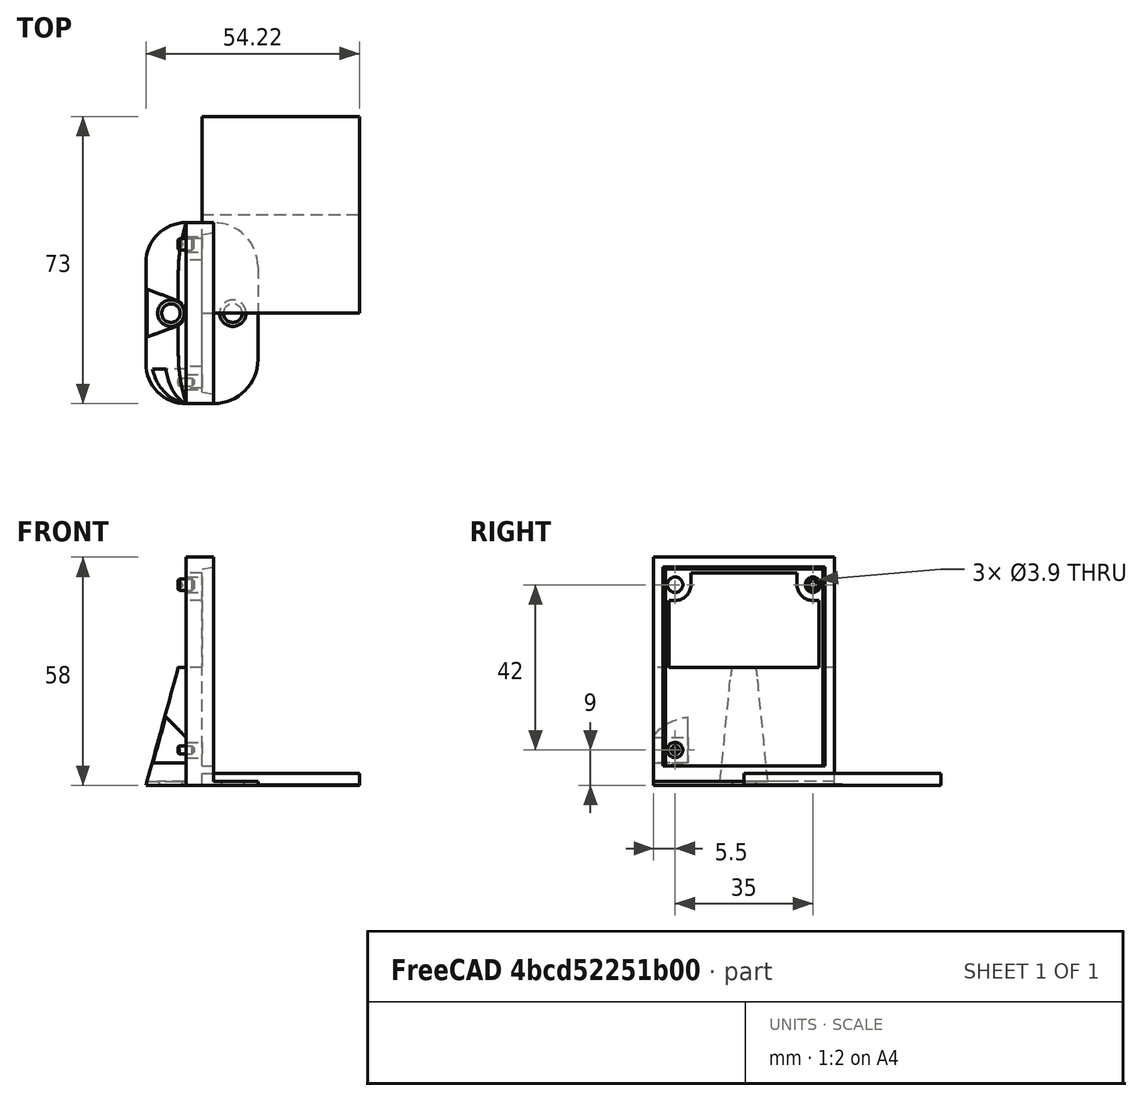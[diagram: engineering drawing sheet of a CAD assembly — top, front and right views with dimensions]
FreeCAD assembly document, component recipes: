
FREECAD ASSEMBLY — COMPONENT RECIPES ("HorizonMirror")

This assembly document has 2 components, labeled P0..P1 below (a component is one placed body or linked part). 1 of them carries a construction recipe — the FreeCAD feature program that regenerates the part from scratch, quoted from this document or its linked companion documents; the rest are supplied as boundary geometry only. No exploded tour is included for this assembly.
COMPONENT P0 — geometry summary ("Mirror"; no construction recipe available for this part):
  bounding box: 50.0 x 40.0 x 3.0 mm
  tessellated surface: 44 triangles
  volume: 6100 mm^3 (102% of its bounding box)
  symmetry: 2-fold rotationally symmetric about the x axis; 2-fold rotationally symmetric about the y axis; 2-fold rotationally symmetric about the z axis; mirror-symmetric across its x mid-plane, y mid-plane, z mid-plane
COMPONENT P1 — recipe-attached ("HorizonMirrorFrame", modeled in this document).
Construction recipe (the document's own serialized feature program — sketch geometry with constraints, then the solid features built on it; lengths are millimeters unless a unit is written):

FEATURE [PartDesign::Plane] DatumPlane  label="Plane_BaseBottom"
  AttachmentSupport = -> [XY_Plane004]
  Length = 60
  MapMode = 5
  ResizeMode = 0
  Width = 60
FEATURE [PartDesign::Plane] DatumPlane001  label="Plane_BaseTop"
  AttachmentOffset = pos=(0,0,1) rot=(0,0,1;0rad)
  AttachmentSupport = -> [DatumPlane]
  Length = 60
  MapMode = 5
  Placement = pos=(0,0,1) rot=(0,0,1;0rad)
  ResizeMode = 0
  Width = 60
  expr: .AttachmentOffset.Base.z = <<Dimensions>>.horizon_mirror_base_thickness
FEATURE [Sketcher::SketchObject] Sketch
  ArcFitTolerance = 0
  AttachmentSupport = -> [DatumPlane001]
  FullyConstrained = true
  MakeInternals = false
  MapMode = 5
  Placement = pos=(0,0,1) rot=(0,0,1;0rad)
  expr: Constraints[0] = <<Dimensions>>.horizon_mirror_screw_diameter
  expr: Constraints[5] = <<Dimensions>>.horizon_mirror_countersink_diameter * 0.5 + <<Dimensions>>.horizon_mirror_base_width + <<Dimensions>>.horizon_mirror_mirror_thickness * 0.5
  sketch-geometry (2):
    g0: Circle CenterX=-7.86 CenterY=0 CenterZ=0 NormalX=0 NormalY=0 NormalZ=1 AngleXU=0 Radius=1.5
    g1: Circle CenterX=7.86 CenterY=0 CenterZ=0 NormalX=0 NormalY=0 NormalZ=1 AngleXU=0 Radius=1.5
  constraints (6):
    c: Diameter(g0) = 3
    c: Equal(g0,g1)
    c: PointOnObject(g0,g-1)
    c: Symmetric(g0,g1,g-1)
    c: Distance(g0,g1) = 15.72  'hole_distance'
    c: Distance(g-1,g0) = 7.86
FEATURE [PartDesign::Plane] DatumPlane002  label="Plane_MirrorBack"
  AttachmentSupport = -> [YZ_Plane004]
  Length = 60
  MapMode = 2
  Placement = pos=(0,0,0) rot=(0.57735,0.57735,0.57735;2.0944rad)
  ResizeMode = 0
  Width = 60
FEATURE [PartDesign::Plane] DatumPlane003  label="Plane_FrameFront"
  AttachmentOffset = pos=(0,0,3) rot=(0,0,1;0rad)
  AttachmentSupport = -> [DatumPlane002]
  Length = 60
  MapMode = 5
  Placement = pos=(3,0,0) rot=(0.57735,0.57735,0.57735;2.0944rad)
  ResizeMode = 0
  Width = 60
  expr: .AttachmentOffset.Base.z = <<Dimensions>>.horizon_mirror_mirror_thickness
FEATURE [PartDesign::Plane] DatumPlane004  label="Plane_FrameBack"
  AttachmentOffset = pos=(0,0,-7) rot=(0,0,1;0rad)
  AttachmentSupport = -> [DatumPlane003]
  Length = 60
  MapMode = 5
  Placement = pos=(-4,0,0) rot=(0.57735,0.57735,0.57735;2.0944rad)
  ResizeMode = 0
  Width = 60
  expr: .AttachmentOffset.Base.z = -<<Dimensions>>.mirror_frame_thickness
FEATURE [Sketcher::SketchObject] Sketch001  label="Sketch_Base"
  ArcFitTolerance = 0
  AttachmentSupport = -> [DatumPlane]
  ExternalGeometry = -> [Sketch,DatumPlane004,DatumPlane003]
  FullyConstrained = true
  MakeInternals = false
  MapMode = 5
  expr: Constraints[10] = <<Dimensions>>.horizon_mirror_mirror_width + 2 * <<Dimensions>>.mirror_frame_width
  expr: Constraints[15] = <<Dimensions>>.horizon_mirror_countersink_diameter / 2 + <<Dimensions>>.horizon_mirror_base_width
  expr: Constraints[19] = <<Dimensions>>.horizon_mirror_countersink_diameter / 2 + <<Dimensions>>.horizon_mirror_base_width
  sketch-geometry (11):
    g0: LineSegment StartX=14.22 StartY=11.78 StartZ=0 EndX=14.22 EndY=-11.78 EndZ=0
    g1: GeomPoint [constr] X=-4 Y=23 Z=0
    g2: LineSegment StartX=-4 StartY=-23 StartZ=0 EndX=3 EndY=-23 EndZ=0
    g3: LineSegment StartX=-4 StartY=23 StartZ=0 EndX=3 EndY=23 EndZ=0
    g4: ArcOfCircle CenterX=3 CenterY=-11.78 CenterZ=0 NormalX=0 NormalY=0 NormalZ=1 AngleXU=0 Radius=11.22 StartAngle=4.71239 EndAngle=6.28319
    g5: ArcOfCircle CenterX=3 CenterY=11.78 CenterZ=0 NormalX=0 NormalY=0 NormalZ=1 AngleXU=0 Radius=11.22 StartAngle=0 EndAngle=1.5708
    g6: LineSegment StartX=-14.22 StartY=12.78 StartZ=0 EndX=-14.22 EndY=-12.78 EndZ=0
    g7: ArcOfCircle CenterX=-4 CenterY=12.78 CenterZ=0 NormalX=0 NormalY=0 NormalZ=1 AngleXU=0 Radius=10.22 StartAngle=1.5708 EndAngle=3.14159
    g8: ArcOfCircle CenterX=-4 CenterY=-12.78 CenterZ=0 NormalX=0 NormalY=0 NormalZ=1 AngleXU=0 Radius=10.22 StartAngle=3.14159 EndAngle=4.71239
    g9: LineSegment StartX=3 StartY=23 StartZ=0 EndX=3 EndY=-23 EndZ=0
    g10: LineSegment StartX=-4 StartY=23 StartZ=0 EndX=-4 EndY=-23 EndZ=0
  constraints (24):
    c: Horizontal(g2)
    c: Coincident(g3,g1)
    c: PointOnObject(g3,g-5)
    c: PointOnObject(g2,g-5)
    c: Tangent(g0,g4) = 1.5708
    c: Tangent(g2,g4) = -1.5708
    c: Tangent(g0,g5) = 1.5708
    c: Tangent(g3,g5) = 1.5708
    c: Vertical(g0)
    c: Equal(g5,g4)
    c: DistanceY(g2,g3) = 46
    c: PointOnObject(g2,g-6)
    c: Vertical(g6)
    c: Tangent(g6,g7) = -1.5708
    c: Tangent(g6,g8) = -1.5708
    c: DistanceX(g6,g-3) = 6.36
    c: Symmetric(g3,g2,g-1)
    c: Tangent(g7,g3) = 1.5708
    c: Tangent(g8,g2) = -1.5708
    c: DistanceX(g-4,g0) = 6.36
    c: Coincident(g9,g3)
    c: Coincident(g9,g2)
    c: Coincident(g10,g3)
    c: Coincident(g10,g2)
FEATURE [PartDesign::SubShapeBinder] Binder001  label="Binder_AdjustmentScrew"
  BindCopyOnChange = 0
  BindMode = 0
  ClaimChildren = false
  Context = -> Part001 [Body001.Hole001.Binder001.]
  Fuse = false
  MakeFace = true
  OffsetFill = false
  OffsetIntersection = false
  OffsetJoinType = 0
  OffsetOpenResult = false
  PartialLoad = false
  Relative = true
  Support = -> [Sketch006]
  _Version = 2
FEATURE [PartDesign::Plane] DatumPlane006  label="Plane_Top"
  AttachmentOffset = pos=(0,0,58) rot=(0,0,1;0rad)
  AttachmentSupport = -> [XY_Plane004]
  Length = 60
  MapMode = 5
  Placement = pos=(0,0,58) rot=(0,0,1;0rad)
  ResizeMode = 0
  Width = 60
  expr: .AttachmentOffset.Base.z = <<Dimensions>>.horizon_mirror_mirror_offset + <<Dimensions>>.horizon_mirror_mirror_height + <<Dimensions>>.mirror_frame_width
FEATURE [Sketcher::SketchObject] Sketch010  label="Sketch_ScrewAccess"
  ArcFitTolerance = 0
  AttachmentSupport = -> [DatumPlane001]
  ExternalGeometry = -> [Sketch]
  FullyConstrained = true
  MakeInternals = false
  MapMode = 5
  Placement = pos=(0,0,1) rot=(0,0,1;0rad)
  expr: Constraints[5] = <<Dimensions>>.horizon_mirror_countersink_diameter / 2 + <<Dimensions>>.clearance_loose_fit
  sketch-geometry (4):
    g0: LineSegment StartX=-26.6253 StartY=10.6717 StartZ=0 EndX=-6.62531 EndY=3.39229 EndZ=0
    g1: ArcOfCircle CenterX=-7.86 CenterY=0 CenterZ=0 NormalX=0 NormalY=0 NormalZ=1 AngleXU=0 Radius=3.61 StartAngle=5.06145 EndAngle=7.50492
    g2: LineSegment StartX=-6.62531 StartY=-3.39229 StartZ=0 EndX=-26.6253 EndY=-10.6717 EndZ=0
    g3: LineSegment StartX=-26.6253 StartY=-10.6717 StartZ=0 EndX=-26.6253 EndY=10.6717 EndZ=0
  constraints (9):
    c: Tangent(g0,g1) = 1.5708
    c: Tangent(g1,g2) = 1.5708
    c: Coincident(g2,g3)
    c: Coincident(g3,g0)
    c: Coincident(g1,g-3)
    c: Radius(g1) = 3.61
    c: DistanceX(g0,g0) = 20
    c: Symmetric(g2,g0,g-1)
    c: Angle(g0,g2) = 0.698132
FEATURE [PartDesign::SubShapeBinder] Binder005  label="Binder_BaseFront"
  BindCopyOnChange = 0
  BindMode = 0
  ClaimChildren = false
  Context = -> <external Sextant.FCStd>#Assembly [HorizonMirror.Base.Body001.Binder005.]
  Fuse = false
  MakeFace = true
  OffsetFill = false
  OffsetIntersection = false
  OffsetJoinType = 0
  OffsetOpenResult = false
  PartialLoad = false
  Relative = true
  Support = -> [Sketch001[Edge3,Edge2,Edge1,Edge9]]
  _Version = 2
FEATURE [PartDesign::Plane] DatumPlane007  label="Plane_ViewCenter"
  AttachmentOffset = pos=(0,0,30) rot=(0,0,1;0rad)
  AttachmentSupport = -> [XY_Plane004]
  Length = 60
  MapMode = 5
  Placement = pos=(0,0,30) rot=(0,0,1;0rad)
  ResizeMode = 0
  Width = 60
  expr: .AttachmentOffset.Base.z = <<Dimensions>>.view_center_offset_hor
FEATURE [Sketcher::SketchObject] Sketch009  label="Sketch_LoftTop"
  ArcFitTolerance = 0
  AttachmentSupport = -> [DatumPlane007]
  ExternalGeometry = -> [DatumPlane004,DatumPlane003]
  FullyConstrained = true
  MakeInternals = false
  MapMode = 5
  Placement = pos=(0,0,30) rot=(0,0,1;0rad)
  expr: Constraints[2] = <<Dimensions>>.horizon_mirror_mirror_width + 2 * <<Dimensions>>.mirror_frame_width
  sketch-geometry (4):
    g0: LineSegment StartX=-4 StartY=23 StartZ=0 EndX=-4 EndY=-23 EndZ=0
    g1: LineSegment StartX=-6 StartY=10 StartZ=0 EndX=-6 EndY=-10 EndZ=0
    g2: ArcOfCircle CenterX=37.25 CenterY=10 CenterZ=0 NormalX=0 NormalY=0 NormalZ=1 AngleXU=0 Radius=43.25 StartAngle=2.83629 EndAngle=3.14159
    g3: ArcOfCircle CenterX=37.25 CenterY=-10 CenterZ=0 NormalX=0 NormalY=0 NormalZ=1 AngleXU=0 Radius=43.25 StartAngle=3.14159 EndAngle=3.44689
  constraints (10):
    c: PointOnObject(g2,g-3)
    c: Symmetric(g2,g3,g-1)
    c: Distance(g0) = 46
    c: Symmetric(g1,g1,g-1)
    c: Tangent(g2,g1) = -1.5708
    c: Tangent(g3,g1) = -1.5708
    c: DistanceY(g1,g1) = 20
    c: DistanceX(g1,g3) = 2
    c: Coincident(g0,g3)
    c: Coincident(g2,g0)
FEATURE [PartDesign::SubShapeBinder] Binder006  label="Binder_FrameBase"
  BindCopyOnChange = 0
  BindMode = 0
  ClaimChildren = false
  Context = -> <external Sextant.FCStd>#Assembly [HorizonMirror.Base.Body001.Binder006.]
  Fuse = false
  MakeFace = true
  OffsetFill = false
  OffsetIntersection = false
  OffsetJoinType = 0
  OffsetOpenResult = false
  PartialLoad = false
  Relative = true
  Support = -> [Sketch001[Edge10,Edge8,Edge9,Edge4]]
  _Version = 2
FEATURE [PartDesign::Pad] Pad006  label="Pad_Frame"
  Direction = (0,0,1)
  Length = 10
  Length2 = 10
  Profile = -> Binder006 [Face1]
  Suppressed = false
  Type = 3
  UpToFace = -> DatumPlane006
FEATURE [PartDesign::Pad] Pad007  label="Pad_BaseFront"
  BaseFeature = -> Pad006
  Direction = (0,0,1)
  Length = 10
  Length2 = 10
  Profile = -> Binder005 [Face1]
  Suppressed = false
  Type = 3
  UpToFace = -> DatumPlane001
FEATURE [PartDesign::SubShapeBinder] Binder004  label="Binder_BaseBack"
  BindCopyOnChange = 0
  BindMode = 0
  ClaimChildren = false
  Context = -> Part001 [Body001.Binder004.]
  Fuse = false
  MakeFace = true
  OffsetFill = false
  OffsetIntersection = false
  OffsetJoinType = 0
  OffsetOpenResult = false
  PartialLoad = false
  Relative = true
  Support = -> [Sketch001[Edge7,Edge10,Edge6,Edge5]]
  _Version = 2
FEATURE [PartDesign::AdditiveLoft] AdditiveLoft  label="Loft_BackSupport"
  BaseFeature = -> Pad007
  Closed = false
  Profile = -> Binder004 [Face1]
  Ruled = false
  Sections = -> [Sketch009]
  Suppressed = false
FEATURE [PartDesign::Pocket] Pocket002  label="Pocket_ScrewAccess"
  BaseFeature = -> AdditiveLoft
  Direction = (0,0,-1)
  Length = 5
  Length2 = 5
  Profile = -> Sketch010
  ReferenceAxis = -> Sketch010 [N_Axis]
  Reversed = true
  Suppressed = false
  Type = 1
FEATURE [PartDesign::Hole] Hole  label="Hole_Attachment"
  BaseFeature = -> Pocket002
  CustomThreadClearance = 0
  Depth = 86.1294
  DepthType = 1
  Diameter = 3.4
  DrillForDepth = false
  DrillPoint = 1
  DrillPointAngle = 118
  HoleCutCountersinkAngle = 90
  HoleCutCustomValues = false
  HoleCutDepth = 0
  HoleCutDiameter = 6.72
  HoleCutType = 2
  ModelThread = false
  Profile = -> Sketch
  Suppressed = false
  Tapered = false
  TaperedAngle = 90
  ThreadClass = 0
  ThreadDepth = 86.1294
  ThreadDepthType = 0
  ThreadDirection = 0
  ThreadFit = 0
  ThreadSize = 9
  ThreadType = 1
  Threaded = false
  UseCustomThreadClearance = false
  expr: HoleCutDiameter = <<Dimensions>>.horizon_mirror_countersink_diameter
  expr: ThreadSize = <<Dimensions>>.horizon_mirror_screw_type
FEATURE [Sketcher::SketchObject] Sketch015  label="Sketch_Mirror"
  ArcFitTolerance = 0
  AttachmentSupport = -> [DatumPlane002]
  ExternalGeometry = -> [DatumPlane007]
  FullyConstrained = true
  MakeInternals = false
  MapMode = 5
  Placement = pos=(0,0,0) rot=(0.57735,0.57735,0.57735;2.0944rad)
  expr: Constraints[5] = <<Dimensions>>.horizon_mirror_mirror_offset
  expr: Constraints[8] = <<Dimensions>>.horizon_mirror_mirror_width
  expr: Constraints[9] = <<Dimensions>>.horizon_mirror_mirror_height
  sketch-geometry (7):
    g0: LineSegment StartX=-20 StartY=55 StartZ=0 EndX=20 EndY=55 EndZ=0
    g1: LineSegment StartX=20 StartY=5 StartZ=0 EndX=-20 EndY=5 EndZ=0
    g2: LineSegment StartX=-20 StartY=30 StartZ=0 EndX=20 EndY=30 EndZ=0
    g3: LineSegment StartX=-20 StartY=5 StartZ=0 EndX=-20 EndY=30 EndZ=0
    g4: LineSegment StartX=-20 StartY=30 StartZ=0 EndX=-20 EndY=55 EndZ=0
    g5: LineSegment StartX=20 StartY=55 StartZ=0 EndX=20 EndY=30 EndZ=0
    g6: LineSegment StartX=20 StartY=30 StartZ=0 EndX=20 EndY=5 EndZ=0
  constraints (19):
    c: Coincident(g0,g5)
    c: Coincident(g6,g1)
    c: Coincident(g1,g3)
    c: Coincident(g4,g0)
    c: Horizontal(g1)
    c: DistanceY(g-1,g6) = 5
    c: PointOnObject(g2,g-3)
    c: Symmetric(g0,g0,g-2)
    c: DistanceX(g0,g0) = 40
    c: DistanceY(g3,g4) = 50
    c: Coincident(g3,g4)
    c: Vertical(g3)
    c: Vertical(g4)
    c: Coincident(g5,g6)
    c: Vertical(g5)
    c: Vertical(g6)
    c: Coincident(g3,g2)
    c: Coincident(g5,g2)
    c: PointOnObject(g2,g-3)
FEATURE [Sketcher::SketchObject] Sketch006  label="Sketch_Clips"
  ArcFitTolerance = 0
  AttachmentSupport = -> [DatumPlane004]
  ExternalGeometry = -> [Sketch015]
  FullyConstrained = true
  MakeInternals = false
  MapMode = 5
  Placement = pos=(-4,0,0) rot=(0.57735,0.57735,0.57735;2.0944rad)
  expr: Constraints[0] = <<Dimensions>>.mirror_adjustment_screw_diameter
  expr: Constraints[22] = <<Dimensions>>.mirror_clip_edge_distance + <<Dimensions>>.mirror_clip_width / 2
  expr: Constraints[28] = <<Dimensions>>.mirror_clip_edge_distance
  sketch-geometry (10):
    g0: Circle CenterX=17.5 CenterY=51 CenterZ=0 NormalX=0 NormalY=0 NormalZ=1 AngleXU=0 Radius=1.5
    g1: Circle CenterX=-17.5 CenterY=9 CenterZ=0 NormalX=0 NormalY=0 NormalZ=1 AngleXU=0 Radius=1.5
    g2: Circle CenterX=-17.5 CenterY=51 CenterZ=0 NormalX=0 NormalY=0 NormalZ=1 AngleXU=0 Radius=1.5
    g3: LineSegment [constr] StartX=17.5 StartY=51 StartZ=0 EndX=17.5 EndY=55 EndZ=0
    g4: LineSegment [constr] StartX=17.5 StartY=51 StartZ=0 EndX=20 EndY=51 EndZ=0
    g5: LineSegment [constr] StartX=-17.5 StartY=51 StartZ=0 EndX=-20 EndY=51 EndZ=0
    g6: LineSegment [constr] StartX=-17.5 StartY=51 StartZ=0 EndX=-17.5 EndY=55 EndZ=0
    g7: LineSegment [constr] StartX=-17.5 StartY=9 StartZ=0 EndX=-17.5 EndY=5 EndZ=0
    g8: LineSegment [constr] StartX=-17.5 StartY=9 StartZ=0 EndX=-20 EndY=9 EndZ=0
    g9: GeomPoint [constr] X=19 Y=51 Z=0
  constraints (29):
    c: Diameter(g0) = 3
    c: Equal(g0,g1)
    c: Equal(g2,g0)
    c: Coincident(g3,g0)
    c: PointOnObject(g3,g-8)
    c: Vertical(g3)
    c: Coincident(g4,g0)
    c: Horizontal(g4)
    c: Coincident(g5,g2)
    c: PointOnObject(g5,g-3)
    c: Horizontal(g5)
    c: Coincident(g6,g2)
    c: PointOnObject(g6,g-8)
    c: Vertical(g6)
    c: Coincident(g7,g1)
    c: PointOnObject(g7,g-5)
    c: Coincident(g8,g1)
    c: PointOnObject(g8,g-4)
    c: Horizontal(g8)
    c: Vertical(g7)
    c: Equal(g7,g3)
    c: Equal(g3,g6)
    c: DistanceY(g6,g6) = 4
    c: Equal(g4,g5)
    c: Equal(g5,g8)
    c: PointOnObject(g4,g-7)
    c: PointOnObject(g9,g4)
    c: PointOnObject(g9,g0)
    c: Distance(g9,g4) = 1
FEATURE [Sketcher::SketchObject] Sketch011
  ArcFitTolerance = 0
  AttachmentSupport = -> [DatumPlane004]
  ExternalGeometry = -> [Sketch006]
  FullyConstrained = true
  MakeInternals = false
  MapMode = 5
  Placement = pos=(-4,0,0) rot=(0.57735,0.57735,0.57735;2.0944rad)
  expr: Constraints[12] = <<Dimensions>>.mirror_clip_width + 2 * <<Dimensions>>.clearance_loose_fit
  expr: Constraints[13] = <<Dimensions>>.mirror_clip_width / 2 + <<Dimensions>>.clearance_loose_fit
  sketch-geometry (6):
    g0: LineSegment StartX=-44.25 StartY=12.25 StartZ=0 EndX=-14.25 EndY=12.25 EndZ=0
    g1: LineSegment StartX=-14.25 StartY=12.25 StartZ=0 EndX=-14.25 EndY=5.75 EndZ=0
    g2: LineSegment StartX=-14.25 StartY=5.75 StartZ=0 EndX=-44.25 EndY=5.75 EndZ=0
    g3: LineSegment StartX=-44.25 StartY=5.75 StartZ=0 EndX=-44.25 EndY=12.25 EndZ=0
    g4: GeomPoint [constr] X=-14.25 Y=9 Z=0
    g5: LineSegment [constr] StartX=-17.5 StartY=9 StartZ=0 EndX=-14.25 EndY=9 EndZ=0
  constraints (15):
    c: Coincident(g2,g3)
    c: Coincident(g0,g3)
    c: Coincident(g1,g2)
    c: Coincident(g0,g1)
    c: Coincident(g5,g-3)
    c: Coincident(g5,g4)
    c: Symmetric(g1,g0,g4)
    c: Horizontal(g5)
    c: Vertical(g1)
    c: Horizontal(g0)
    c: Horizontal(g2)
    c: Vertical(g3)
    c: DistanceY(g1,g1) = 6.5
    c: DistanceX(g5,g5) = 3.25
    c: DistanceX(g2,g2) = 30
FEATURE [PartDesign::SubShapeBinder] Binder007  label="Binder_Mirror"
  BindCopyOnChange = 0
  BindMode = 0
  ClaimChildren = false
  Context = -> Part001 [Body001.Binder007.]
  Fuse = false
  MakeFace = true
  OffsetFill = false
  OffsetIntersection = false
  OffsetJoinType = 0
  OffsetOpenResult = false
  PartialLoad = false
  Relative = true
  Support = -> [Sketch015[Edge7,Edge1,Edge2,Edge4,Edge5,Edge6]]
  _Version = 2
FEATURE [PartDesign::Pocket] Pocket  label="Pocket_Mirror"
  BaseFeature = -> Hole
  Direction = (-1,0,0)
  Length = 5
  Length2 = 5
  Profile = -> Binder007
  Reversed = true
  Suppressed = false
  Type = 1
FEATURE [PartDesign::Draft] Draft
  Angle = 10
  Base = -> Pocket [Face21,Face27,Face22,Face25]
  BaseFeature = -> Pocket
  NeutralPlane = -> DatumPlane002
  SupportTransform = false
  Suppressed = false
FEATURE [PartDesign::SubShapeBinder] Binder008  label="Binder_MirrorOnlyGlass"
  BindCopyOnChange = 0
  BindMode = 0
  ClaimChildren = false
  Context = -> <external Sextant.FCStd>#Assembly [HorizonMirror.Base.Body001.Binder008.]
  Fuse = false
  MakeFace = true
  OffsetFill = false
  OffsetIntersection = false
  OffsetJoinType = 0
  OffsetOpenResult = false
  PartialLoad = false
  Relative = true
  Support = -> [Sketch015[Edge7,Edge1,Edge3,Edge2]]
  _Version = 2
FEATURE [Sketcher::SketchObject] Sketch003  label="Sketch_Window"
  ArcFitTolerance = 0
  AttachmentSupport = -> [DatumPlane002]
  ExternalGeometry = -> [Sketch006,Binder008]
  FullyConstrained = true
  MakeInternals = false
  MapMode = 5
  Placement = pos=(0,0,0) rot=(0.57735,0.57735,0.57735;2.0944rad)
  expr: Constraints[13] = <<Dimensions>>.horizon_mirror_frame_lip_width
  expr: Constraints[14] = <<Dimensions>>.horizon_mirror_frame_lip_width
  expr: Constraints[15] = <<Dimensions>>.horizon_mirror_frame_lip_width
  sketch-geometry (11):
    g0: LineSegment StartX=-19 StartY=30 StartZ=0 EndX=-19 EndY=47 EndZ=0
    g1: LineSegment StartX=-13.5 StartY=54 StartZ=0 EndX=13.5 EndY=54 EndZ=0
    g2: LineSegment StartX=19 StartY=47 StartZ=0 EndX=19 EndY=30 EndZ=0
    g3: GeomPoint [constr] X=19 Y=54 Z=0
    g4: ArcOfCircle CenterX=-17.5 CenterY=51 CenterZ=0 NormalX=0 NormalY=0 NormalZ=1 AngleXU=0 Radius=4 StartAngle=4.71239 EndAngle=6.28319
    g5: ArcOfCircle CenterX=17.5 CenterY=51 CenterZ=0 NormalX=0 NormalY=0 NormalZ=1 AngleXU=0 Radius=4 StartAngle=3.14159 EndAngle=4.71239
    g6: LineSegment StartX=-19 StartY=30 StartZ=0 EndX=19 EndY=30 EndZ=0
    g7: LineSegment StartX=-13.5 StartY=51 StartZ=0 EndX=-13.5 EndY=54 EndZ=0
    g8: LineSegment StartX=13.5 StartY=51 StartZ=0 EndX=13.5 EndY=54 EndZ=0
    g9: LineSegment StartX=-17.5 StartY=47 StartZ=0 EndX=-19 EndY=47 EndZ=0
    g10: LineSegment StartX=17.5 StartY=47 StartZ=0 EndX=19 EndY=47 EndZ=0
  constraints (28):
    c: Coincident(g4,g-3)
    c: Coincident(g5,g-4)
    c: Vertical(g0)
    c: Horizontal(g1)
    c: Vertical(g2)
    c: Vertical(g3,g2)
    c: Horizontal(g1,g3)
    c: Equal(g5,g4)
    c: Radius(g4) = 4
    c: PointOnObject(g0,g-6)
    c: PointOnObject(g2,g-6)
    c: Coincident(g6,g0)
    c: Coincident(g6,g2)
    c: DistanceX(g2,g-8) = 1
    c: DistanceX(g-6,g0) = 1
    c: DistanceY(g1,g-7) = 1
    c: Vertical(g7)
    c: Coincident(g7,g1)
    c: Tangent(g7,g4) = -1.5708
    c: Vertical(g8)
    c: Coincident(g1,g8)
    c: Tangent(g8,g5) = 1.5708
    c: Horizontal(g9)
    c: Coincident(g0,g9)
    c: Tangent(g9,g4) = 1.5708
    c: Horizontal(g10)
    c: Coincident(g2,g10)
    c: Tangent(g10,g5) = -1.5708
FEATURE [PartDesign::Pocket] Pocket004  label="Pocket_Window"
  BaseFeature = -> Draft
  Direction = (-1,0,0)
  Length = 5
  Length2 = 5
  Profile = -> Sketch003
  ReferenceAxis = -> Sketch003 [N_Axis]
  Suppressed = false
  Type = 1
FEATURE [PartDesign::Pocket] Pocket003
  BaseFeature = -> Pocket004
  Direction = (-1,0,0)
  Length = 5
  Length2 = 5
  Profile = -> Sketch011
  ReferenceAxis = -> Sketch011 [N_Axis]
  Refine = true
  Suppressed = false
  Type = 1
FEATURE [PartDesign::Draft] Draft001
  Angle = 45
  Base = -> Pocket003 [Face25]
  BaseFeature = -> Pocket003
  NeutralPlane = -> DatumPlane004
  Reversed = true
  SupportTransform = false
  Suppressed = false
FEATURE [PartDesign::Hole] Hole001  label="Holes_AdjustmentScrew"
  BaseFeature = -> Draft001
  CustomThreadClearance = 0
  Depth = 160.19
  DepthType = 1
  Diameter = 3.4
  DrillForDepth = false
  DrillPoint = 1
  DrillPointAngle = 118
  HoleCutCountersinkAngle = 90
  HoleCutCustomValues = false
  HoleCutDepth = 4
  HoleCutDiameter = 3.9
  HoleCutType = 1
  ModelThread = false
  Profile = -> Binder001
  Reversed = true
  Suppressed = false
  Tapered = false
  TaperedAngle = 90
  ThreadClass = 0
  ThreadDepth = 160.19
  ThreadDepthType = 0
  ThreadDirection = 0
  ThreadFit = 0
  ThreadSize = 9
  ThreadType = 1
  Threaded = false
  UseCustomThreadClearance = false
  expr: HoleCutDepth = <<Dimensions>>.mirror_adjustment_ti_L
  expr: HoleCutDiameter = <<Dimensions>>.mirror_adjustment_ti_D
  expr: ThreadSize = <<Dimensions>>.mirror_adjustment_screw_type
FEATURE [PartDesign::Body] Body001  label="HorizonMirrorFrameBody"
  AllowCompound = false
  Group = -> [DatumPlane,DatumPlane001,DatumPlane007,DatumPlane002,DatumPlane003,DatumPlane004,DatumPlane006,Sketch001,Binder006,Pad006,Binder005,Sketch,Sketch009,Sketch010,Pad007,Binder004,AdditiveLoft,Pocket002,Hole,Sketch015,Sketch006,Binder007,Pocket,Draft,Binder008,Sketch003,Binder001,Sketch011,Pocket004,Pocket003,Draft001,Hole001]
  Origin = -> Origin004
  Tip = -> Hole001
PROVENANCE & LICENSES
A FreeCAD (.FCStd) document from a public repository crawl; recipes are the document's own serialized feature recipes (and, for linked parts, companion documents' recipes).
License: gpl-3.0.
